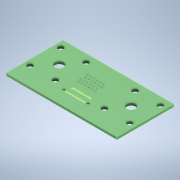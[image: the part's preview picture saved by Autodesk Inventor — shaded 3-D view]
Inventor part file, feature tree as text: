
AUTODESK INVENTOR PART (.ipt)
format: ipt  version: 2021 (Build 250183000, 183)  size: 580,096 bytes
history: native  units: mm
features: sketch x8, projected_geometry x7, extrude x4, hole x4, plane x2
ambient origin geometry x8: Origin, YZ Plane, XZ Plane, XY Plane, X Axis, Y Axis, Z Axis, Center Point
bodies: Solid1 (feature_tree)
feature tree (25):
  extrude  "Extrusion1"  Depth=34.75mm
  hole  "Hole1"  [1 undecoded]
  plane  "Work Plane1"
  plane  "Work Plane2"
  hole  "Hole2"  [1 undecoded]
  hole  "Hole3"  [1 undecoded]
  extrude  "Extrusion2"  Depth=10.0mm
  hole  "Hole4"  [1 undecoded]
  extrude  "Extrusion3"  Depth=1.1mm
  extrude  "Extrusion4"  Depth=1.1mm
  sketch  "Sketch1"  dims[d0=67.75mm d1=34.75mm]
  sketch  "Sketch2"  dims[d2=1.6mm d3=0.0mm d4=3.2mm]
  projected_geometry  "Projected Loop1"
  sketch  "Sketch3"  dims[d5=22.0mm d6=44.0mm]
  projected_geometry  "Projected Loop2"
  sketch  "Sketch4"  dims[d7=5.5mm d8=6.0mm d9=10.0mm d10=5.7mm d11=14.3117mm d12=8.0mm d13=20.594885mm d14=60.0mm d16=2.0mm d17=10.0mm d19=10.0mm]
  projected_geometry  "Projected Loop3"
  sketch  "Sketch5"  dims[d22=60.0mm d24=10.0mm d25=2.0mm d26=10.0mm]
  projected_geometry  "Projected Loop4"
  sketch  "Sketch6"  dims[d28=60.0mm d30=10.0mm d32=60.0mm d34=10.0mm d35=2.0mm d36=10.0mm]
  projected_geometry  "Projected Loop5"
  sketch  "Sketch7"  dims[d38=60.0mm d40=10.0mm d42=60.0mm d44=10.0mm d46=60.0mm d48=10.0mm d49=2.0mm d50=10.0mm d51=1.0mm d52=2.0mm]
  projected_geometry  "Projected Loop6"
  sketch  "Sketch8"  dims[d53=1.0mm d54=2.0mm d55=2.0mm d56=2.2mm d57=8.0mm d58=0.8mm d59=6.0mm d60=10.0mm d61=5.7mm d62=14.3117mm d63=5.0mm d64=0.0mm d65=1.5mm d66=14.8mm d67=10.25mm d68=1.45mm d69=6.0mm d70=4.0mm d71=2.0mm d72=90.0deg d73=8.0mm d74=20.594885mm d75=0.5mm d76=1.1mm d77=150.0mm d79=0.8mm d80=20.0mm d82=3.8mm d85=0.01mm d86=0.0mm d87=18.8mm d88=61.0mm d89=30.0mm d90=30.0mm d91=3.4mm d92=6.0mm d93=6.3mm d94=2.0mm d95=90.0deg d96=8.0mm d97=20.594885mm d98=10.0mm d99=10.0mm d100=18.2mm d101=8.2mm d102=10.4mm d103=19.5mm d104=5.0mm d105=0.005mm d106=0.0mm d107=14.2mm d108=0.005mm d109=0.0mm d110=5.0mm d111=1.1mm]
  projected_geometry  "Projected Loop7"
note: 4 required parameter values undecoded (feature->parameter linkage not recoverable at this tier; creation-order binding heuristic only, values carry confidence <= 0.55)
